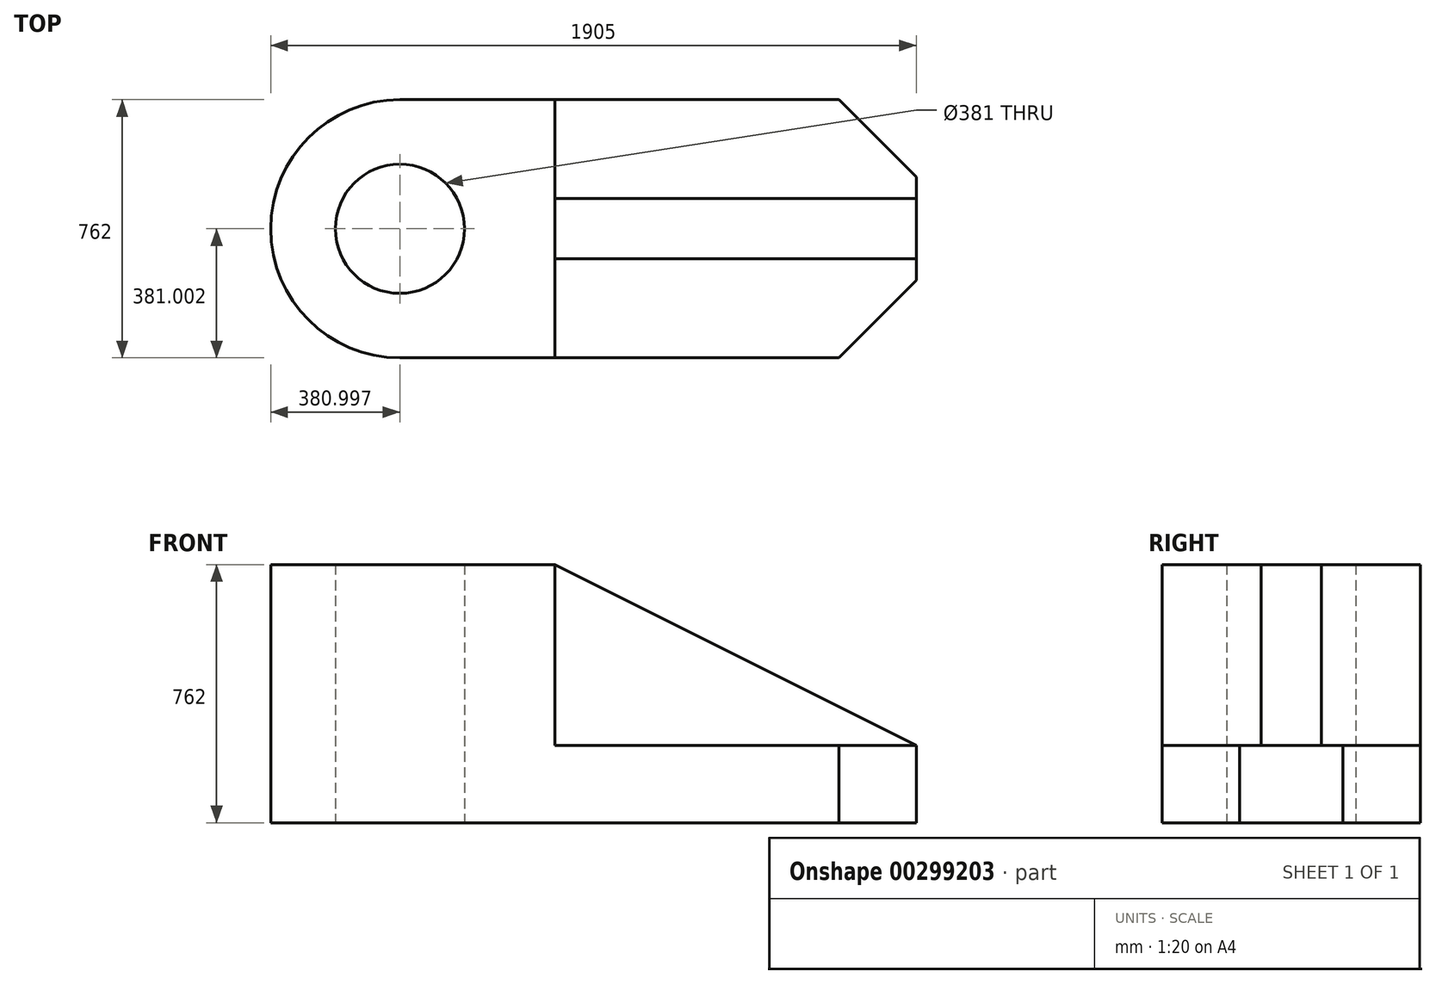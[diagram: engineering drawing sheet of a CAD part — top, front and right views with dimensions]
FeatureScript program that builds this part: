
annotation { "Feature Type Name" : "Feature", "Feature Type Description" : "" }
export const myFeature = defineFeature(function(context is Context, id is Id, definition is map)
    precondition{}
    {
        {
            var Q0;
            Q0=qCreatedBy(makeId("Top.planeOp"),FACE);
            var sketch = newSketch(context, id + "F0", { "sketchPlane" : qUnion([Q0])});
            skCircle(sketch, "E0", {"center": v(-62.63, 12.41) * mm, "radius": 190.5 * mm});
            skCircle(sketch, "E1", {"center": v(-62.63, 12.41) * mm, "radius": 381 * mm});
            skLineSegment(sketch, "E2", {"start": v(-62.63, 393.41) * mm, "end": v(394.57, 393.41) * mm});
            skLineSegment(sketch, "E3", {"start": v(-62.63, -368.59) * mm, "end": v(394.57, -368.59) * mm});
            skLineSegment(sketch, "E4", {"start": v(394.57, -368.59) * mm, "end": v(1461.37, -368.59) * mm});
            skLineSegment(sketch, "E5", {"start": v(394.57, 393.41) * mm, "end": v(394.57, -368.59) * mm});
            skLineSegment(sketch, "E6", {"start": v(394.57, 393.41) * mm, "end": v(1461.37, 393.41) * mm});
            skLineSegment(sketch, "E7", {"start": v(1461.37, 393.41) * mm, "end": v(1461.37, -368.59) * mm});
            skSolve(sketch);
        }
        {
            var Q0;
            Q0=makeQuery(id+"F0.imprint","IMPRINT",FACE,{"disambiguationData":[TD([[makeQuery(id+"F0.imprint","IMPRINT",EDGE,{"derivedFrom":sQuery(id+"F0.wireOp",EDGE,"E0")}),-1.0]])]});
            var Q1;
            {var subQ0=sQuery(id+"F0.wireOp",EDGE,"E2");Q1=makeQuery(id+"F0.imprint","IMPRINT",FACE,{"disambiguationData":[TD([[makeQuery(id+"F0.imprint","IMPRINT",EDGE,{"derivedFrom":subQ0}),-1.0]])]});}
            extrude(context, id + "F1", {"entities" : qUnion([Q0, Q1]), "depth" : 762 * mm});
        }
        {
            var Q0;
            Q0=makeQuery(id+"F0.imprint","IMPRINT",FACE,{"disambiguationData":[TD([[makeQuery(id+"F0.imprint","IMPRINT",EDGE,{"derivedFrom":sQuery(id+"F0.wireOp",EDGE,"E4")}),1.0]])]});
            extrude(context, id + "F2", {"entities" : qUnion([Q0]), "operationType" : NewBodyOperationType.ADD, "depth" : 228.6 * mm});
        }
        {
            var Q0;
            Q0=makeQuery(id+"F2.opExtrude","SWEPT_EDGE",EDGE,{"disambiguationData":[OSD([sQuery(id+"F0.wireOp",EDGE,"E6"),sQuery(id+"F0.wireOp",EDGE,"E7")])]});
            var Q1;
            Q1=makeQuery(id+"F2.opExtrude","SWEPT_EDGE",EDGE,{"disambiguationData":[OSD([sQuery(id+"F0.wireOp",EDGE,"E4"),sQuery(id+"F0.wireOp",EDGE,"E7")])]});
            chamfer(context, id + "F3", {"entities" : qUnion([Q0, Q1]), "width" : 228.6 * mm, "tangentPropagation" : true});
        }
        {
            var Q0;
            Q0=makeQuery(id+"F2.opExtrude","CAP_FACE",FACE,{"disambiguationData":[OSD([sQuery(id+"F0.wireOp",EDGE,"E4"),sQuery(id+"F0.wireOp",EDGE,"E5"),sQuery(id+"F0.wireOp",EDGE,"E6"),sQuery(id+"F0.wireOp",EDGE,"E7")])],"isStart":false});
            var sketch = newSketch(context, id + "F4", { "sketchPlane" : qUnion([Q0])});
            skLineSegment(sketch, "E8", {"start": v(394.57, 12.41) * mm, "end": v(394.57, 101.31) * mm});
            skLineSegment(sketch, "E9", {"start": v(394.57, 12.41) * mm, "end": v(394.57, -76.49) * mm});
            skLineSegment(sketch, "E10", {"start": v(394.57, 101.31) * mm, "end": v(1461.37, 101.31) * mm});
            skLineSegment(sketch, "E11", {"start": v(394.57, -76.49) * mm, "end": v(1461.37, -76.49) * mm});
            skLineSegment(sketch, "E12", {"start": v(1461.37, 101.31) * mm, "end": v(1461.37, -76.49) * mm});
            skSolve(sketch);
        }
        {
            var Q0;
            Q0=makeQuery(id+"F4.imprint","IMPRINT",FACE,{"disambiguationData":[TD([[makeQuery(id+"F4.imprint","IMPRINT",EDGE,{"derivedFrom":sQuery(id+"F4.wireOp",EDGE,"E8")}),1.0]])]});
            extrude(context, id + "F5", {"entities" : qUnion([Q0]), "operationType" : NewBodyOperationType.ADD, "depth" : 533.4 * mm});
        }
        {
            var Q0;
            Q0=makeQuery(id+"F5.opExtrude","SWEPT_FACE",FACE,{"disambiguationData":[OSD([sQuery(id+"F4.wireOp",EDGE,"E11")])]});
            var sketch = newSketch(context, id + "F6", { "sketchPlane" : qUnion([Q0])});
            skLineSegment(sketch, "E13", {"start": v(394.57, 762) * mm, "end": v(1461.37, 228.6) * mm});
            skLineSegment(sketch, "E14", {"start": v(1461.37, 228.6) * mm, "end": v(1461.37, 762) * mm});
            skLineSegment(sketch, "E15", {"start": v(1461.37, 762) * mm, "end": v(394.57, 762) * mm});
            skSolve(sketch);
        }
        {
            var Q0;
            Q0=makeQuery(id+"F6.imprint","IMPRINT",FACE,{"disambiguationData":[TD([[makeQuery(id+"F6.imprint","IMPRINT",EDGE,{"derivedFrom":sQuery(id+"F6.wireOp",EDGE,"E13")}),1.0]])]});
            extrude(context, id + "F7", {"entities" : qUnion([Q0]), "operationType" : NewBodyOperationType.REMOVE, "oppositeDirection" : true, "depth" : 2540 * mm});
        }
    });
